# Revit family: Deca_Chuveiro com tubo de parede_Banho Luxo_1992.CT
name_source: partatom
category: Plumbing Fixtures
units: mm (PartAtom-declared; Revit-internal decimal feet)

## family parameters
Cut with Voids When Loaded = No
Host = Face
Part Type = Normal
Room Calculation Point = No
Round Connector Dimension = Use Radius
Shared = No

## types (5) — shared parameters
Aprovado por = quattroD
Atendimento ao Cliente = 0800-0117073
Categoria = CHUVEIROS E DUCHAS
Composição Anel Vedação = -
Composição Assento = -
Composição Básica = Liga de Cobre (bronze e latão),Plásticos de Engenharia,Elastômeros
Composição Componente = -
Consumo = -
Cor Interna = -
Cor Secundária = -
Cores Componente = -
Criado por = quattroD
Código Pai = 1992.CT
Default Elevation = 2200 mm
Description = Chuveiro com tubo de parede
Diâmetro Água Fria = 15 mm  [stored 0.0492126 ft]
Informações Complementares = -
Itens de Instalação = -
Linha = Banho Luxo
Manufacturer = Deca
Norma = NBR15206
Pressão máx. funcionamento = 40 MCA
Pressão mín. Aquec. Acúmulo = 2 MCA
Pressão mín. Aquec. Passagem = 6 MCA
Pressão mín. funcionamento = 2 MCA
Raio Água Fria = 8 mm  [stored 0.0262467 ft]
Saída de Esgoto = -
Segmento = Banheiro Luxo
Tipo de dispositivo economizador = Sim
Tipo de mecanismo utilizado = -
Tipo de rosca de entrada = BSP NBR 8133
Tipo de rosca de saída = -
URL = www.deca.com.br
Vazão na Pressão máx. (L/min) = 40
Vazão na Pressão mín. (L/min) = 12
zero-valued in all types: HWFU

## per-type parameters (varying)
| type | Acompanha o Produto | Cor Principal | Material | Model | Peso Líquido (Kg) |
| 1992.C.CT_Cromado | Acompanha Deca confort (12l/min) + Parafuso e bucha para fixação | Cromado | Deca_Cromado | 1992.C.CT | 5.07 |
| 1992.BL.CT.MT_Black Matte | Acompanha Deca confort  (12l/min)+ Parafuso e bucha para fixação | Black Matte | Deca_Black Matte | 1992.BL.CT.MT | 4.932 |
| 1992.CT.CT.MT_Corten | Acompanha Deca confort (12l/min) + Parafuso e bucha para fixação | Corten | Deca_Corten | 1992.CT.CT.MT | 4.932 |
| 1992.GL.CT.MT_Gold Matte | Acompanha Deca confort (12l/min) + Parafuso e bucha para fixação | Gold Matte | Deca_Gold Matte | 1992.GL.CT.MT | 4.932 |
| 1992.GL.CT.RD_Red Gold | Acompanha Deca confort (12l/min) + Parafuso e bucha para fixação | Red Gold | Deca_Red Gold | 1992.GL.CT.RD | 5.07 |

note: source unit labels omitted for Vazão na Pressão máx. (L/min), Vazão na Pressão mín. (L/min) — the stored unit's dimension contradicts the parameter name (converter mislabeling)

note: [stored X ft] marks values corroborated as IEEE doubles in the binary element streams (Revit-internal decimal feet)

## geometry (parser evidence)
native form markers: Sweep x2
no freeform markers — native parametric forms only
